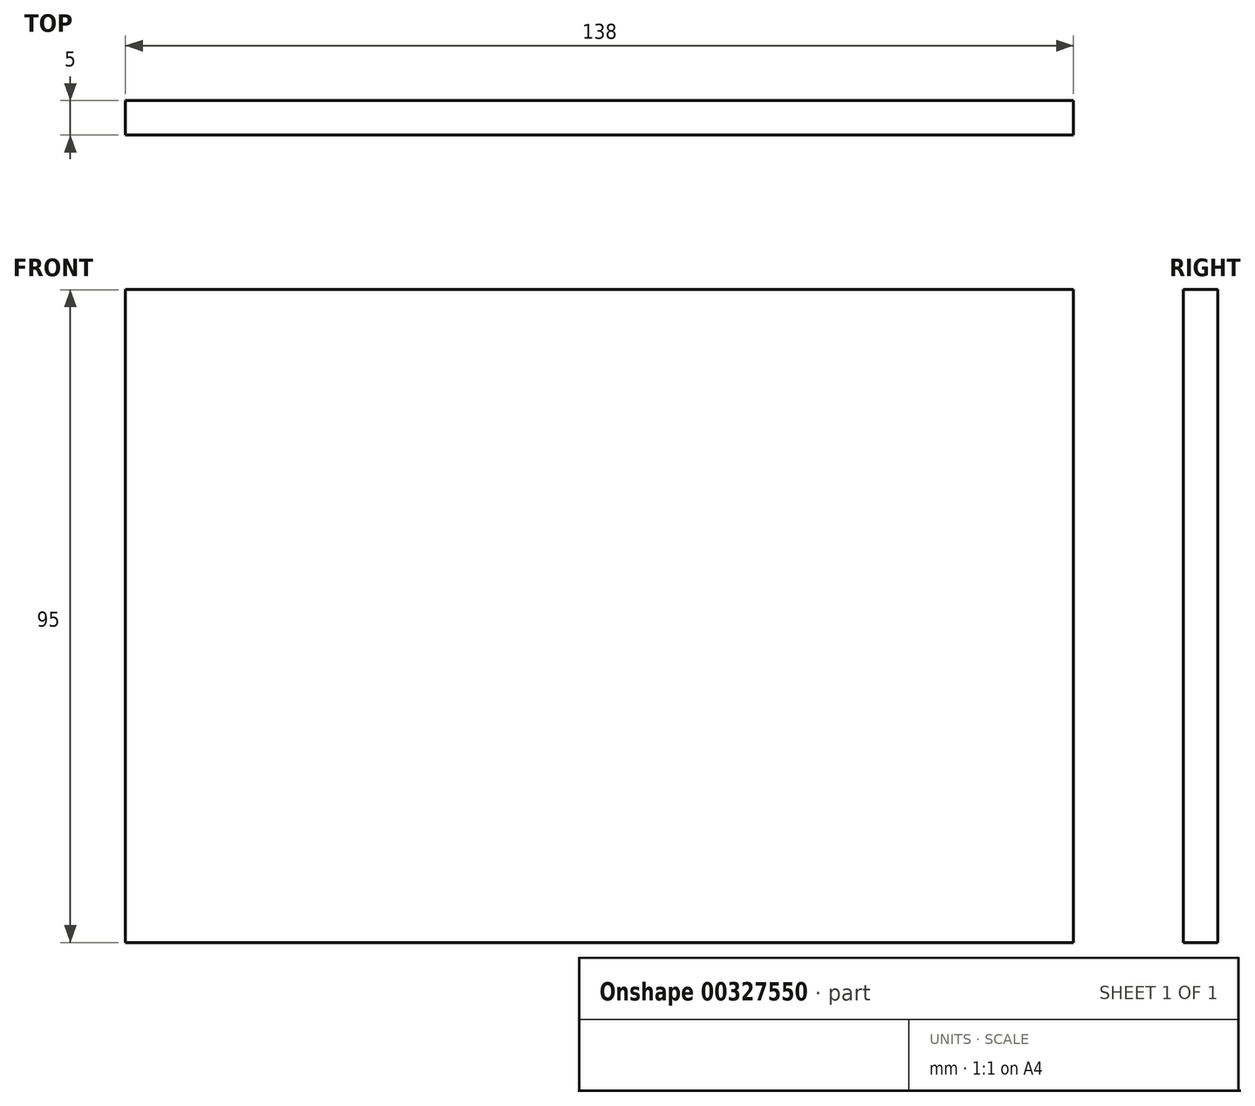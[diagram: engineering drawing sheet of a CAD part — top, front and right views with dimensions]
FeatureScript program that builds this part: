
annotation { "Feature Type Name" : "Feature", "Feature Type Description" : "" }
export const myFeature = defineFeature(function(context is Context, id is Id, definition is map)
    precondition{}
    {
        {
            var Q0;
            Q0=qCreatedBy(makeId("Front.planeOp"),FACE);
            var sketch = newSketch(context, id + "F0", { "sketchPlane" : qUnion([Q0])});
            skLineSegment(sketch, "E0.bottom", {"start": v(-380.77, -137.52) * mm, "end": v(-242.77, -137.52) * mm});
            skLineSegment(sketch, "E0.top", {"start": v(-380.77, -232.52) * mm, "end": v(-242.77, -232.52) * mm});
            skLineSegment(sketch, "E0.left", {"start": v(-380.77, -137.52) * mm, "end": v(-380.77, -232.52) * mm});
            skLineSegment(sketch, "E0.right", {"start": v(-242.77, -137.52) * mm, "end": v(-242.77, -232.52) * mm});
            skSolve(sketch);
        }
        {
            var Q0;
            Q0=makeQuery(id+"F0.imprint","IMPRINT",FACE,{"disambiguationData":[TD([[makeQuery(id+"F0.imprint","IMPRINT",EDGE,{"derivedFrom":sQuery(id+"F0.wireOp",EDGE,"E0.bottom")}),-1.0]])]});
            extrude(context, id + "F1", {"entities" : qUnion([Q0]), "depth" : 5 * mm});
        }
    });
